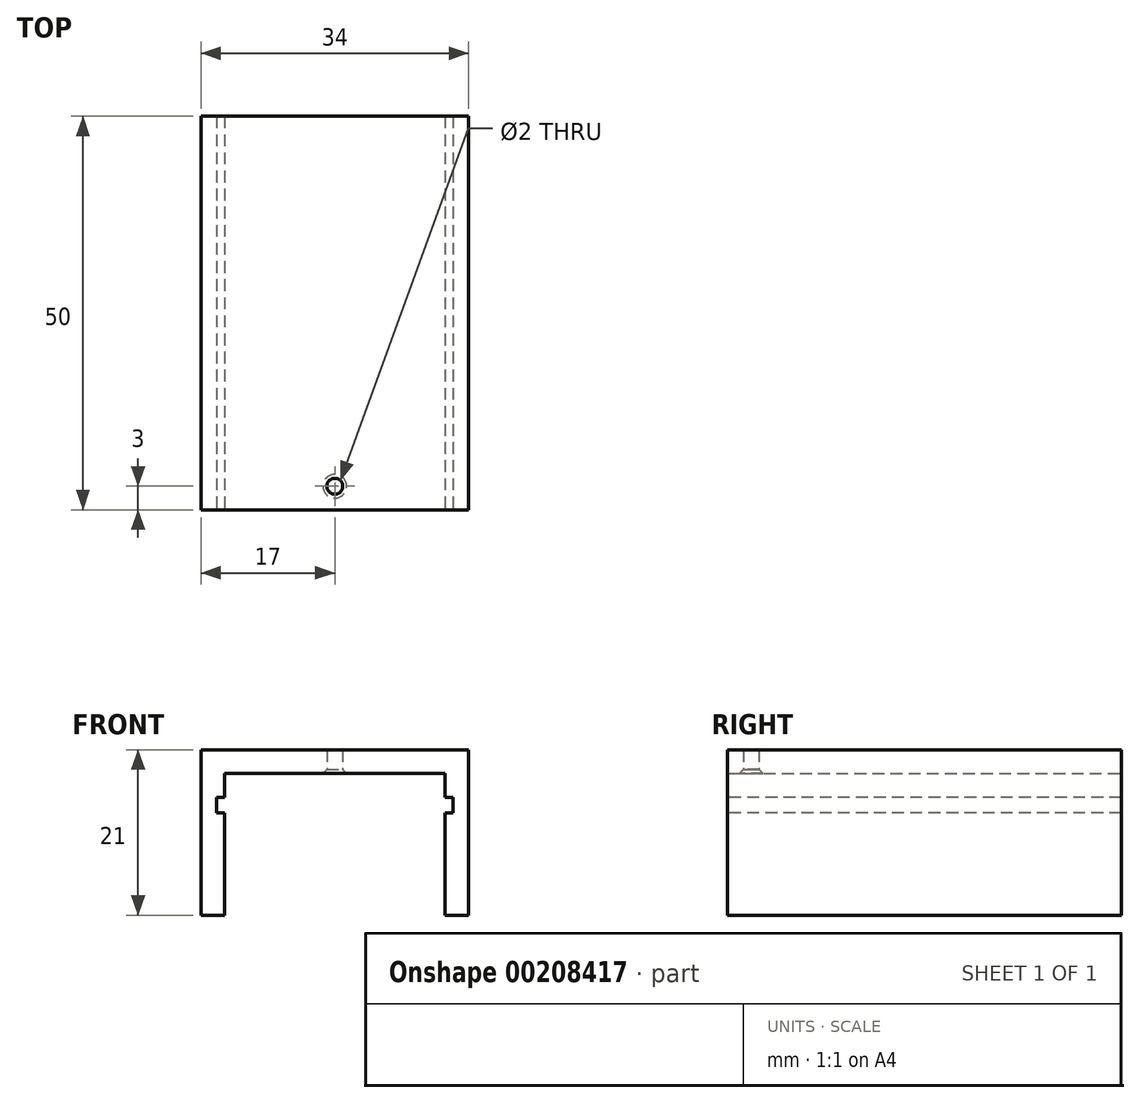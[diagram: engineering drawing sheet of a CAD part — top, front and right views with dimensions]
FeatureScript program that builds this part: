
annotation { "Feature Type Name" : "Feature", "Feature Type Description" : "" }
export const myFeature = defineFeature(function(context is Context, id is Id, definition is map)
    precondition{}
    {
        {
            var Q0;
            Q0=qCreatedBy(makeId("Front.planeOp"),FACE);
            var sketch = newSketch(context, id + "F0", { "sketchPlane" : qUnion([Q0])});
            skLineSegment(sketch, "E0.bottom", {"start": v(0, 0) * mm, "end": v(-3, 0) * mm});
            skLineSegment(sketch, "E0.top", {"start": v(0, -21) * mm, "end": v(-3, -21) * mm});
            skLineSegment(sketch, "E0.left", {"start": v(0, 0) * mm, "end": v(0, -21) * mm});
            skLineSegment(sketch, "E0.right", {"start": v(-3, 0) * mm, "end": v(-3, -21) * mm});
            skLineSegment(sketch, "E1.bottom", {"start": v(0, 0) * mm, "end": v(28, 0) * mm});
            skLineSegment(sketch, "E1.top", {"start": v(0, -3) * mm, "end": v(28, -3) * mm});
            skLineSegment(sketch, "E1.left", {"start": v(0, 0) * mm, "end": v(0, -3) * mm});
            skLineSegment(sketch, "E1.right", {"start": v(28, 0) * mm, "end": v(28, -3) * mm});
            skLineSegment(sketch, "E2.bottom", {"start": v(28, 0) * mm, "end": v(31, 0) * mm});
            skLineSegment(sketch, "E2.top", {"start": v(28, -21) * mm, "end": v(31, -21) * mm});
            skLineSegment(sketch, "E2.left", {"start": v(28, 0) * mm, "end": v(28, -21) * mm});
            skLineSegment(sketch, "E2.right", {"start": v(31, 0) * mm, "end": v(31, -21) * mm});
            skSolve(sketch);
        }
        {
            var Q0;
            Q0=makeQuery(id+"F0.imprint","IMPRINT",FACE,{"disambiguationData":[TD([[makeQuery(id+"F0.imprint","IMPRINT",EDGE,{"derivedFrom":sQuery(id+"F0.wireOp",EDGE,"E0.bottom")}),1.0]])]});
            var Q1;
            {var subQ0=sQuery(id+"F0.wireOp",EDGE,"E1.bottom");Q1=makeQuery(id+"F0.imprint","IMPRINT",FACE,{"disambiguationData":[TD([[makeQuery(id+"F0.imprint","IMPRINT",EDGE,{"derivedFrom":subQ0}),-1.0]])]});}
            var Q2;
            {var subQ1=sQuery(id+"F0.wireOp",EDGE,"E2.bottom");Q2=makeQuery(id+"F0.imprint","IMPRINT",FACE,{"disambiguationData":[TD([[makeQuery(id+"F0.imprint","IMPRINT",EDGE,{"derivedFrom":subQ1}),-1.0]])]});}
            extrude(context, id + "F1", {"entities" : qUnion([Q0, Q1, Q2]), "depth" : 50 * mm});
        }
        {
            var Q0;
            Q0=makeQuery(id+"F1.opExtrude","CAP_FACE",FACE,{"disambiguationData":[OSD([sQuery(id+"F0.wireOp",EDGE,"E0.bottom"),sQuery(id+"F0.wireOp",EDGE,"E0.top"),sQuery(id+"F0.wireOp",EDGE,"E0.left"),sQuery(id+"F0.wireOp",EDGE,"E0.right"),sQuery(id+"F0.wireOp",EDGE,"E1.bottom"),sQuery(id+"F0.wireOp",EDGE,"E1.top"),sQuery(id+"F0.wireOp",EDGE,"E2.bottom"),sQuery(id+"F0.wireOp",EDGE,"E2.top"),sQuery(id+"F0.wireOp",EDGE,"E2.left"),sQuery(id+"F0.wireOp",EDGE,"E2.right")])],"isStart":false});
            var sketch = newSketch(context, id + "F2", { "sketchPlane" : qUnion([Q0])});
            skLineSegment(sketch, "E3.bottom", {"start": v(0, -6) * mm, "end": v(-1, -6) * mm});
            skLineSegment(sketch, "E3.top", {"start": v(0, -8) * mm, "end": v(-1, -8) * mm});
            skLineSegment(sketch, "E3.left", {"start": v(0, -6) * mm, "end": v(0, -8) * mm});
            skLineSegment(sketch, "E3.right", {"start": v(-1, -6) * mm, "end": v(-1, -8) * mm});
            skLineSegment(sketch, "E4", {"start": v(14, -3) * mm, "end": v(14, -22.04) * mm});
            skLineSegment(sketch, "E5.MirrorCS", {"start": v(28, -6) * mm, "end": v(29, -6) * mm});
            skLineSegment(sketch, "E6.MirrorCS", {"start": v(29, -6) * mm, "end": v(29, -8) * mm});
            skLineSegment(sketch, "E7.MirrorCS", {"start": v(28, -6) * mm, "end": v(28, -8) * mm});
            skLineSegment(sketch, "E8.MirrorCS", {"start": v(28, -8) * mm, "end": v(29, -8) * mm});
            skSolve(sketch);
        }
        {
            var Q0;
            Q0=makeQuery(id+"F2.imprint","IMPRINT",FACE,{"disambiguationData":[TD([[makeQuery(id+"F2.imprint","IMPRINT",EDGE,{"derivedFrom":sQuery(id+"F2.wireOp",EDGE,"E3.bottom")}),1.0]])]});
            var Q1;
            Q1=makeQuery(id+"F2.imprint","IMPRINT",FACE,{"disambiguationData":[TD([[makeQuery(id+"F2.imprint","IMPRINT",EDGE,{"derivedFrom":sQuery(id+"F2.wireOp",EDGE,"E5.MirrorCS")}),-1.0]])]});
            extrude(context, id + "F3", {"entities" : qUnion([Q0, Q1]), "operationType" : NewBodyOperationType.REMOVE, "oppositeDirection" : true, "depth" : 50 * mm});
        }
        {
            var Q0;
            Q0=makeQuery(id+"F1.opExtrude","SWEPT_FACE",FACE,{"disambiguationData":[OSD([sQuery(id+"F0.wireOp",EDGE,"E1.top")])]});
            var sketch = newSketch(context, id + "F4", { "sketchPlane" : qUnion([Q0])});
            skLineSegment(sketch, "E9", {"start": v(14, 50) * mm, "end": v(14, 47) * mm});
            skPoint(sketch, "E10", {"position": v(14, 47) * mm});
            skLineSegment(sketch, "E11", {"start": v(0, 25) * mm, "end": v(58.81, 25) * mm});
            skSolve(sketch);
        }
        {
            var Q0;
            Q0=sQuery(id+"F4.wireOp",VERTEX,"E10");
            var Q1;
            Q1=makeQuery(id+"F1.opExtrude","SWEPT_BODY",BODY,{"disambiguationData":[OSD([sQuery(id+"F0.wireOp",EDGE,"E0.bottom"),sQuery(id+"F0.wireOp",EDGE,"E0.top"),sQuery(id+"F0.wireOp",EDGE,"E0.left"),sQuery(id+"F0.wireOp",EDGE,"E0.right"),sQuery(id+"F0.wireOp",EDGE,"E1.bottom"),sQuery(id+"F0.wireOp",EDGE,"E1.top"),sQuery(id+"F0.wireOp",EDGE,"E2.bottom"),sQuery(id+"F0.wireOp",EDGE,"E2.top"),sQuery(id+"F0.wireOp",EDGE,"E2.left"),sQuery(id+"F0.wireOp",EDGE,"E2.right")])]});
            hole(context, id + "F5", {"style" : HoleStyle.C_SINK, "endStyle" : HoleEndStyle.THROUGH, "holeDiameter" : 2 * mm, "cSinkDiameter" : 3 * mm, "cSinkAngle" : 90 * degree, "startFromSketch" : true, "locations" : qUnion([Q0]), "scope" : qUnion([Q1]), "isTappedThrough" : true});
        }
    });
